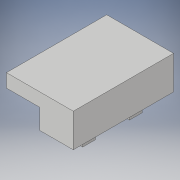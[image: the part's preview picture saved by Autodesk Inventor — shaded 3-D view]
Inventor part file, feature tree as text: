
AUTODESK INVENTOR PART (.ipt)
format: ipt  version: 2019 (Build 230136000, 136)  size: 121,344 bytes
history: native  units: in
note: dims shown in document units (in); Inventor stores cm internally (conversion verified against a paired STEP export)
features: extrude x3, sketch x3
ambient origin geometry x8: Origin, YZ Plane, XZ Plane, XY Plane, X Axis, Y Axis, Z Axis, Center Point
bodies: Solid1 (feature_tree)
feature tree (6):
  extrude  "Extrusion1"  Depth=0.5906in
  extrude  "Extrusion2"  Depth=0.1969in
  extrude  "Extrusion3"  Depth=0.0787in
  sketch  "Sketch1"  dims[d0=0.3937in d1=0.5906in]
  sketch  "Sketch2"  dims[d2=0.1969in d3=0.0in d4=0.1969in]
  sketch  "Sketch3"  dims[d5=0.1969in d6=0.0in d7=0.0787in d8=0.2756in d9=0.0787in d10=0.0in d11=0.002in d12=0.002in d13=0.1181in d14=0.1024in]
